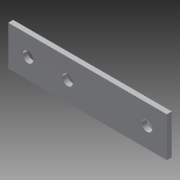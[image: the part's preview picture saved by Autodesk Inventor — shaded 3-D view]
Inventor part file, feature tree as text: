
AUTODESK INVENTOR PART (.ipt)
format: ipt  version: 2013 (Build 170138000, 138)  size: 82,944 bytes
history: native  units: in
note: dims shown in document units (in); Inventor stores cm internally (conversion verified against a paired STEP export)
features: extrude x1, sketch x1
ambient origin geometry x8: Origin, YZ Plane, XZ Plane, XY Plane, X Axis, Y Axis, Z Axis, Center Point
feature tree (2):
  extrude  "Extrusion2"  Depth=4.0in
  sketch  "Sketch1"  dims[d0=1.0in d1=4.0in d2=0.266in d3=0.266in d4=0.875in d5=0.5in d6=0.5in d7=0.5in d10=0.266in d11=1.25in d12=0.125in d13=0.0in d14=0.5in]
